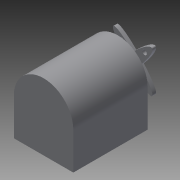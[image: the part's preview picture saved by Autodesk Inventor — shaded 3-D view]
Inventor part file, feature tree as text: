
AUTODESK INVENTOR PART (.ipt)
format: ipt  version: 2014 (Build 180170000, 170)  size: 129,024 bytes
history: native  units: mm
features: extrude x4, sketch x4
ambient origin geometry x8: Origin, YZ Plane, XZ Plane, XY Plane, X Axis, Y Axis, Z Axis, Center Point
bodies: Solid1 (feature_tree)
feature tree (8):
  extrude  "Extrusion1"  Depth=50.0mm TaperAngle=0.0deg
  extrude  "Extrusion2"  Depth=10.0mm TaperAngle=0.0deg
  extrude  "Extrusion3"  Depth=3.0mm
  extrude  "Extrusion4"  Depth=2.5mm
  sketch  "Sketch1"  dims[d0=40.0mm d2=50.0mm d3=0.0mm]
  sketch  "Sketch2"  dims[d4=7.5mm d5=10.0mm d6=0.0mm]
  sketch  "Sketch3"  dims[d7=3.0mm d8=3.0mm]
  sketch  "Sketch4"  dims[d9=3.0mm d10=3.0mm d11=2.5mm d12=0.0mm d13=2.5mm d14=0.0mm]
